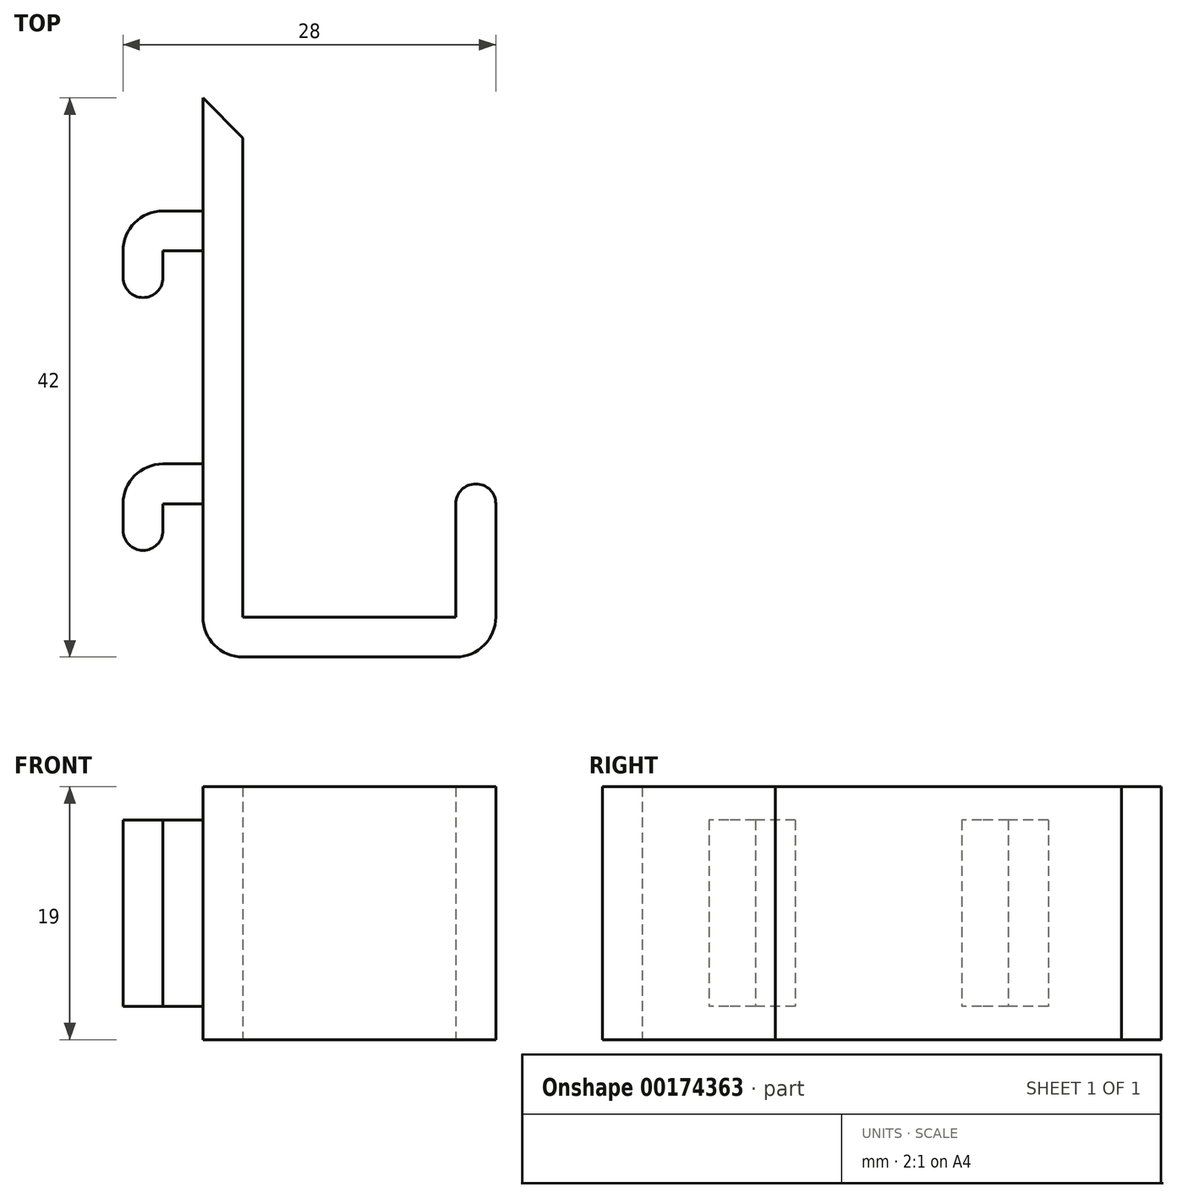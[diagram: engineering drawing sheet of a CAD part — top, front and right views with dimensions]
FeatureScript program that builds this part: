
annotation { "Feature Type Name" : "Feature", "Feature Type Description" : "" }
export const myFeature = defineFeature(function(context is Context, id is Id, definition is map)
    precondition{}
    {
        {
            var Q0;
            Q0=qCreatedBy(makeId("Top.planeOp"),FACE);
            var sketch = newSketch(context, id + "F0", { "sketchPlane" : qUnion([Q0])});
            skLineSegment(sketch, "E0.bottom", {"start": v(1.5, 21) * mm, "end": v(-1.5, 21) * mm});
            skLineSegment(sketch, "E0.top", {"start": v(1.5, -21) * mm, "end": v(-1.5, -21) * mm});
            skLineSegment(sketch, "E0.left", {"start": v(1.5, 21) * mm, "end": v(1.5, -21) * mm});
            skLineSegment(sketch, "E0.right", {"start": v(-1.5, 21) * mm, "end": v(-1.5, -21) * mm});
            skPoint(sketch, "E0.middle", {"position": v(0, 0) * mm});
            skLineSegment(sketch, "E1.bottom", {"start": v(-1.5, -21) * mm, "end": v(20.5, -21) * mm});
            skLineSegment(sketch, "E1.top", {"start": v(-1.5, -18) * mm, "end": v(20.5, -18) * mm});
            skLineSegment(sketch, "E1.left", {"start": v(-1.5, -21) * mm, "end": v(-1.5, -18) * mm});
            skLineSegment(sketch, "E1.right", {"start": v(20.5, -21) * mm, "end": v(20.5, -18) * mm});
            skLineSegment(sketch, "E2.bottom", {"start": v(20.5, -21) * mm, "end": v(17.5, -21) * mm});
            skLineSegment(sketch, "E2.top", {"start": v(20.5, -8) * mm, "end": v(17.5, -8) * mm});
            skLineSegment(sketch, "E2.left", {"start": v(20.5, -21) * mm, "end": v(20.5, -8) * mm});
            skLineSegment(sketch, "E2.right", {"start": v(17.5, -21) * mm, "end": v(17.5, -8) * mm});
            skLineSegment(sketch, "E3", {"start": v(-1.5, 21) * mm, "end": v(1.5, 18) * mm});
            skLineSegment(sketch, "E4.bottom", {"start": v(-1.5, 12.5) * mm, "end": v(-4.5, 12.5) * mm});
            skLineSegment(sketch, "E4.top", {"start": v(-1.5, 9.5) * mm, "end": v(-4.5, 9.5) * mm});
            skLineSegment(sketch, "E4.left", {"start": v(-1.5, 12.5) * mm, "end": v(-1.5, 9.5) * mm});
            skLineSegment(sketch, "E4.right", {"start": v(-4.5, 12.5) * mm, "end": v(-4.5, 9.5) * mm});
            skLineSegment(sketch, "E5.bottom", {"start": v(-1.5, -6.5) * mm, "end": v(-4.5, -6.5) * mm});
            skLineSegment(sketch, "E5.top", {"start": v(-1.5, -9.5) * mm, "end": v(-4.5, -9.5) * mm});
            skLineSegment(sketch, "E5.left", {"start": v(-1.5, -6.5) * mm, "end": v(-1.5, -9.5) * mm});
            skLineSegment(sketch, "E5.right", {"start": v(-4.5, -6.5) * mm, "end": v(-4.5, -9.5) * mm});
            skLineSegment(sketch, "E6.bottom", {"start": v(-4.5, 9.5) * mm, "end": v(-7.5, 9.5) * mm});
            skLineSegment(sketch, "E6.top", {"start": v(-4.5, 7.5) * mm, "end": v(-7.5, 7.5) * mm});
            skLineSegment(sketch, "E6.left", {"start": v(-4.5, 9.5) * mm, "end": v(-4.5, 7.5) * mm});
            skLineSegment(sketch, "E6.right", {"start": v(-7.5, 9.5) * mm, "end": v(-7.5, 7.5) * mm});
            skLineSegment(sketch, "E7.bottom", {"start": v(-4.5, -9.5) * mm, "end": v(-7.5, -9.5) * mm});
            skLineSegment(sketch, "E7.top", {"start": v(-4.5, -11.5) * mm, "end": v(-7.5, -11.5) * mm});
            skLineSegment(sketch, "E7.left", {"start": v(-4.5, -9.5) * mm, "end": v(-4.5, -11.5) * mm});
            skLineSegment(sketch, "E7.right", {"start": v(-7.5, -9.5) * mm, "end": v(-7.5, -11.5) * mm});
            skArc(sketch, "E8", {"start": v(-4.5, 12.5) * mm, "mid": v(-6.62, 11.62) * mm, "end": v(-7.5, 9.5) * mm});
            skArc(sketch, "E9", {"start": v(-7.5, -9.5) * mm, "mid": v(-6.62, -7.38) * mm, "end": v(-4.5, -6.5) * mm});
            skArc(sketch, "E10", {"start": v(-7.5, -11.5) * mm, "mid": v(-6, -13) * mm, "end": v(-4.5, -11.5) * mm});
            skArc(sketch, "E11", {"start": v(-7.5, 7.5) * mm, "mid": v(-6, 6) * mm, "end": v(-4.5, 7.5) * mm});
            skLineSegment(sketch, "E12", {"start": v(17.5, -9.5) * mm, "end": v(20.5, -9.5) * mm});
            skArc(sketch, "E13", {"start": v(20.5, -9.5) * mm, "mid": v(19, -8) * mm, "end": v(17.5, -9.5) * mm});
            skArc(sketch, "E14", {"start": v(-1.5, -18) * mm, "mid": v(-0.62, -20.12) * mm, "end": v(1.5, -21) * mm});
            skArc(sketch, "E15", {"start": v(17.5, -21) * mm, "mid": v(19.62, -20.12) * mm, "end": v(20.5, -18) * mm});
            skSolve(sketch);
        }
        {
            var Q0;
            {var subQ5=sQuery(id+"F0.wireOp",EDGE,"E3");Q0=makeQuery(id+"F0.imprint","IMPRINT",FACE,{"disambiguationData":[TD([[makeQuery(id+"F0.imprint","IMPRINT",EDGE,{"derivedFrom":subQ5}),-1.0]])]});}
            var Q1;
            {var subQ0=sQuery(id+"F0.wireOp",EDGE,"E14");Q1=makeQuery(id+"F0.imprint","IMPRINT",FACE,{"disambiguationData":[TD([[makeQuery(id+"F0.imprint","IMPRINT",EDGE,{"derivedFrom":subQ0}),1.0]])]});}
            var Q2;
            {var subQ1=sQuery(id+"F0.wireOp",EDGE,"E0.left");var subQ3=sQuery(id+"F0.wireOp",EDGE,"E1.top");var subQ4=makeQuery(id+"F0.imprint","INTERSECT",VERTEX,{"derivedFrom":[subQ1,subQ3]});Q2=makeQuery(id+"F0.imprint","IMPRINT",FACE,{"disambiguationData":[TD([[makeQuery(id+"F0.imprint","IMPRINT",EDGE,{"disambiguationData":[TD([[subQ4,-1.0]])],"derivedFrom":subQ3}),-1.0]])]});}
            var Q3;
            {var subQ6=sQuery(id+"F0.wireOp",EDGE,"E12");Q3=makeQuery(id+"F0.imprint","IMPRINT",FACE,{"disambiguationData":[TD([[makeQuery(id+"F0.imprint","IMPRINT",EDGE,{"derivedFrom":subQ6}),-1.0]])]});}
            var Q4;
            {var subQ0=sQuery(id+"F0.wireOp",EDGE,"E15");Q4=makeQuery(id+"F0.imprint","IMPRINT",FACE,{"disambiguationData":[TD([[makeQuery(id+"F0.imprint","IMPRINT",EDGE,{"derivedFrom":subQ0}),1.0]])]});}
            var Q5;
            {var subQ0=sQuery(id+"F0.wireOp",EDGE,"E12");Q5=makeQuery(id+"F0.imprint","IMPRINT",FACE,{"disambiguationData":[TD([[makeQuery(id+"F0.imprint","IMPRINT",EDGE,{"derivedFrom":subQ0}),1.0]])]});}
            extrude(context, id + "F1", {"entities" : qUnion([Q0, Q1, Q2, Q3, Q4, Q5]), "depth" : 9.5 * mm, "hasSecondDirection" : true, "secondDirectionOppositeDirection" : true, "secondDirectionDepth" : 9.5 * mm});
        }
        {
            var Q0;
            Q0=makeQuery(id+"F0.imprint","IMPRINT",FACE,{"disambiguationData":[TD([[makeQuery(id+"F0.imprint","IMPRINT",EDGE,{"derivedFrom":sQuery(id+"F0.wireOp",EDGE,"E4.bottom")}),1.0]])]});
            var Q1;
            Q1=makeQuery(id+"F0.imprint","IMPRINT",FACE,{"disambiguationData":[TD([[makeQuery(id+"F0.imprint","IMPRINT",EDGE,{"derivedFrom":sQuery(id+"F0.wireOp",EDGE,"E4.right")}),-1.0]])]});
            var Q2;
            Q2=makeQuery(id+"F0.imprint","IMPRINT",FACE,{"disambiguationData":[TD([[makeQuery(id+"F0.imprint","IMPRINT",EDGE,{"derivedFrom":sQuery(id+"F0.wireOp",EDGE,"E6.bottom")}),1.0]])]});
            var Q3;
            Q3=makeQuery(id+"F0.imprint","IMPRINT",FACE,{"disambiguationData":[TD([[makeQuery(id+"F0.imprint","IMPRINT",EDGE,{"derivedFrom":sQuery(id+"F0.wireOp",EDGE,"E6.top")}),1.0]])]});
            var Q4;
            Q4=makeQuery(id+"F0.imprint","IMPRINT",FACE,{"disambiguationData":[TD([[makeQuery(id+"F0.imprint","IMPRINT",EDGE,{"derivedFrom":sQuery(id+"F0.wireOp",EDGE,"E7.top")}),1.0]])]});
            var Q5;
            Q5=makeQuery(id+"F0.imprint","IMPRINT",FACE,{"disambiguationData":[TD([[makeQuery(id+"F0.imprint","IMPRINT",EDGE,{"derivedFrom":sQuery(id+"F0.wireOp",EDGE,"E7.bottom")}),1.0]])]});
            var Q6;
            Q6=makeQuery(id+"F0.imprint","IMPRINT",FACE,{"disambiguationData":[TD([[makeQuery(id+"F0.imprint","IMPRINT",EDGE,{"derivedFrom":sQuery(id+"F0.wireOp",EDGE,"E5.right")}),-1.0]])]});
            var Q7;
            Q7=makeQuery(id+"F0.imprint","IMPRINT",FACE,{"disambiguationData":[TD([[makeQuery(id+"F0.imprint","IMPRINT",EDGE,{"derivedFrom":sQuery(id+"F0.wireOp",EDGE,"E5.bottom")}),1.0]])]});
            extrude(context, id + "F2", {"entities" : qUnion([Q0, Q1, Q2, Q3, Q4, Q5, Q6, Q7]), "operationType" : NewBodyOperationType.ADD, "depth" : 7 * mm, "hasSecondDirection" : true, "secondDirectionOppositeDirection" : true, "secondDirectionDepth" : 7 * mm});
        }
    });
